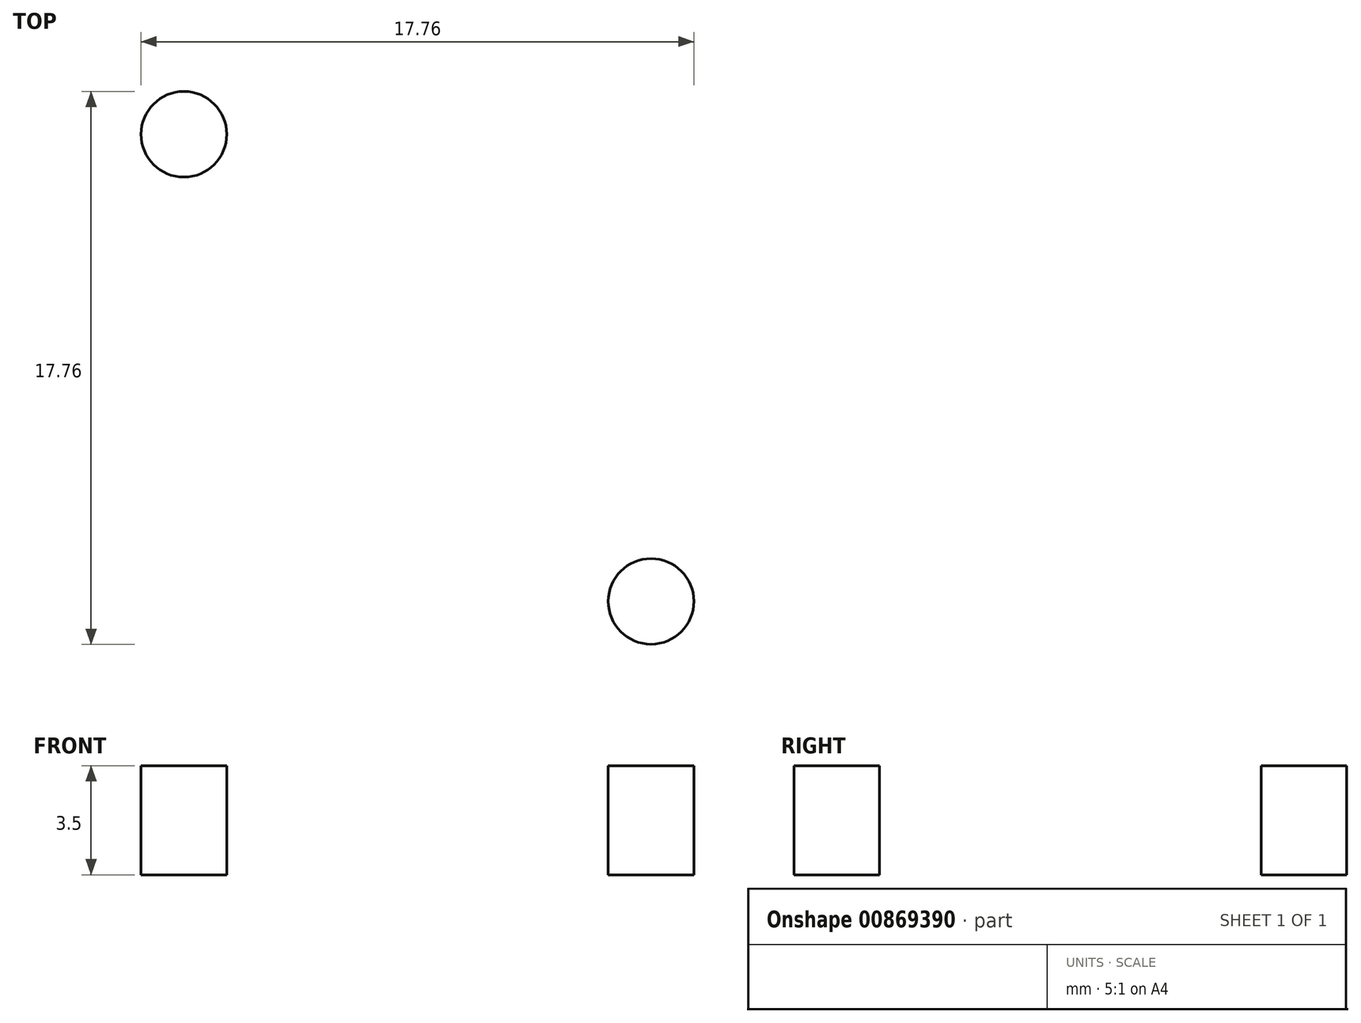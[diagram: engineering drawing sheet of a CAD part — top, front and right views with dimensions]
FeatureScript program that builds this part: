
annotation { "Feature Type Name" : "Feature", "Feature Type Description" : "" }
export const myFeature = defineFeature(function(context is Context, id is Id, definition is map)
    precondition{}
    {
        {
            var Q0;
            Q0=qCreatedBy(makeId("Top.planeOp"),FACE);
            var sketch = newSketch(context, id + "F0", { "sketchPlane" : qUnion([Q0])});
            skLineSegment(sketch, "E0.bottom", {"start": v(0, 0) * mm, "end": v(20, 0) * mm});
            skLineSegment(sketch, "E0.top", {"start": v(0, 20) * mm, "end": v(20, 20) * mm});
            skLineSegment(sketch, "E0.left", {"start": v(0, 0) * mm, "end": v(0, 20) * mm});
            skLineSegment(sketch, "E0.right", {"start": v(20, 0) * mm, "end": v(20, 20) * mm});
            skSolve(sketch);
        }
        {
            var Q0;
            Q0=makeQuery(id+"F0.imprint","IMPRINT",FACE,{"disambiguationData":[TD([[makeQuery(id+"F0.imprint","IMPRINT",EDGE,{"derivedFrom":sQuery(id+"F0.wireOp",EDGE,"E0.bottom")}),1.0]])]});
            extrude(context, id + "F1", {"entities" : qUnion([Q0]), "depth" : 5 * mm, "offsetDistance" : 25 * mm});
        }
        {
            var Q0;
            Q0=makeQuery(id+"F1.opExtrude","CAP_FACE",FACE,{"disambiguationData":[OSD([sQuery(id+"F0.wireOp",EDGE,"E0.bottom"),sQuery(id+"F0.wireOp",EDGE,"E0.top"),sQuery(id+"F0.wireOp",EDGE,"E0.left"),sQuery(id+"F0.wireOp",EDGE,"E0.right")])],"isStart":false});
            var sketch = newSketch(context, id + "F2", { "sketchPlane" : qUnion([Q0])});
            skCircle(sketch, "E1", {"center": v(10, 10) * mm, "radius": 3 * mm});
            skPoint(sketch, "E1.centerSnap0", {"position": v(10, 0) * mm});
            skPoint(sketch, "E1.centerSnap1", {"position": v(0, 10) * mm});
            skLineSegment(sketch, "E2", {"start": v(0, 10) * mm, "end": v(20, 10) * mm, "construction": true});
            skLineSegment(sketch, "E3", {"start": v(10, 20) * mm, "end": v(10, 0) * mm, "construction": true});
            skCircle(sketch, "E4", {"center": v(2.5, 2.5) * mm, "radius": 1.38 * mm});
            skCircle(sketch, "E5.MirrorC", {"center": v(2.5, 17.5) * mm, "radius": 1.38 * mm});
            skCircle(sketch, "E6.MirrorC", {"center": v(17.5, 17.5) * mm, "radius": 1.38 * mm});
            skCircle(sketch, "E7.MirrorC", {"center": v(17.5, 2.5) * mm, "radius": 1.38 * mm});
            skSolve(sketch);
        }
        {
            var Q0;
            Q0=makeQuery(id+"F2.imprint","IMPRINT",FACE,{"disambiguationData":[TD([[makeQuery(id+"F2.imprint","IMPRINT",EDGE,{"derivedFrom":sQuery(id+"F2.wireOp",EDGE,"E1")}),1.0]])]});
            var Q1;
            Q1=makeQuery(id+"F2.imprint","IMPRINT",FACE,{"disambiguationData":[TD([[makeQuery(id+"F2.imprint","IMPRINT",EDGE,{"derivedFrom":sQuery(id+"F2.wireOp",EDGE,"E5.MirrorC")}),-1.0]])]});
            var Q2;
            Q2=makeQuery(id+"F2.imprint","IMPRINT",FACE,{"disambiguationData":[TD([[makeQuery(id+"F2.imprint","IMPRINT",EDGE,{"derivedFrom":sQuery(id+"F2.wireOp",EDGE,"E6.MirrorC")}),1.0]])]});
            var Q3;
            Q3=makeQuery(id+"F2.imprint","IMPRINT",FACE,{"disambiguationData":[TD([[makeQuery(id+"F2.imprint","IMPRINT",EDGE,{"derivedFrom":sQuery(id+"F2.wireOp",EDGE,"E7.MirrorC")}),-1.0]])]});
            var Q4;
            Q4=makeQuery(id+"F2.imprint","IMPRINT",FACE,{"disambiguationData":[TD([[makeQuery(id+"F2.imprint","IMPRINT",EDGE,{"derivedFrom":sQuery(id+"F2.wireOp",EDGE,"E4")}),1.0]])]});
            extrude(context, id + "F3", {"entities" : qUnion([Q0, Q1, Q2, Q3, Q4]), "operationType" : NewBodyOperationType.REMOVE, "oppositeDirection" : true, "depth" : 25 * mm, "offsetDistance" : 25 * mm});
        }
        {
            var Q0;
            Q0=makeQuery(id+"F1.opExtrude","CAP_FACE",FACE,{"disambiguationData":[OSD([sQuery(id+"F0.wireOp",EDGE,"E0.bottom"),sQuery(id+"F0.wireOp",EDGE,"E0.top"),sQuery(id+"F0.wireOp",EDGE,"E0.left"),sQuery(id+"F0.wireOp",EDGE,"E0.right")])],"isStart":false});
            var sketch = newSketch(context, id + "F4", { "sketchPlane" : qUnion([Q0])});
            skCircle(sketch, "E8", {"center": v(10, 10) * mm, "radius": 5 * mm});
            skSolve(sketch);
        }
        {
            var Q0;
            Q0=makeQuery(id+"F4.imprint","IMPRINT",FACE,{"disambiguationData":[TD([[makeQuery(id+"F4.imprint","IMPRINT",EDGE,{"derivedFrom":sQuery(id+"F4.wireOp",EDGE,"E8")}),1.0]])]});
            extrude(context, id + "F5", {"entities" : qUnion([Q0]), "operationType" : NewBodyOperationType.REMOVE, "oppositeDirection" : true, "depth" : 3.5 * mm, "offsetDistance" : 25 * mm});
        }
        {
            var Q0;
            Q0=makeQuery(id+"F1.opExtrude","CAP_FACE",FACE,{"disambiguationData":[OSD([sQuery(id+"F0.wireOp",EDGE,"E0.bottom"),sQuery(id+"F0.wireOp",EDGE,"E0.top"),sQuery(id+"F0.wireOp",EDGE,"E0.left"),sQuery(id+"F0.wireOp",EDGE,"E0.right")])],"isStart":false});
            var sketch = newSketch(context, id + "F6", { "sketchPlane" : qUnion([Q0])});
            skCircle(sketch, "E9", {"center": v(10, 10) * mm, "radius": 7.5 * mm});
            skSolve(sketch);
        }
        {
            var Q0;
            Q0=makeQuery(id+"F6.imprint","IMPRINT",FACE,{"disambiguationData":[TD([[makeQuery(id+"F6.imprint","IMPRINT",EDGE,{"derivedFrom":sQuery(id+"F6.wireOp",EDGE,"E9")}),1.0]])]});
            var Q1;
            Q1 = qSketchRegion(id + "F2", true);
            extrude(context, id + "F7", {"entities" : qUnion([Q0, Q1]), "operationType" : NewBodyOperationType.REMOVE, "oppositeDirection" : true, "depth" : 1.5 * mm, "offsetDistance" : 25 * mm});
        }
    });
